# Revit family: 2093120 Sylvania Lighting Fixture MC2 3-6M 4K DALIEM WHT OPAL Recessed
name_source: partatom
category: Lighting Fixtures
revit_build: Autodesk Revit 2016 (Build: 20150220_1215(x64)
units: mm (PartAtom-declared; Revit-internal decimal feet)

## family parameters
Cut with Voids When Loaded = No
Host = Face
Light Source = Yes
OmniClass Number = 23.80.70.11.17
OmniClass Title = Specialized Lighting by Location or Use
Part Type = Normal
Room Calculation Point = No
Round Connector Dimension = Use Diameter
Shared = No

## types (2) — shared parameters
Apparent Load = 66 VA
Assembly Code = D5020200
AssetType = Fixed
Color Filter = 16777215
Description = 2093120   MC2 3.6M 4K DALIEM WHT OPAL  Continuous lines of LED light, white RAL 9016, direct distribution, trimless detail for a seamless finish, suitable for recessed, semi-recessed, surface-mounted or suspended installation either horizontally or vertically, various accessories available, compact and minimalist design based on the Golden Mean, ideal for offices, meeting rooms, corridors, education facilities, museums and libraries, extruded aluminium body, diffuser: opal, colour temperature: 4000K neutral white, total system power: 66W, total fixture output: 6621lm, luminaire efficacy: 100lm/W, LOR: 100%, colour rendering: Ra >80, LED Chromacity: 1 step MacAdam ellipse, lifetime: 60,000 hours at 90% of the original output (L90), energy class: A++, A+, A, IR/UV free light source without heat radiation, operating voltage: 220-240V / 50-60Hz, drive current: 800mA, electronic driver, DALI dimmable, integral emergency: 3 hour maintained, electrical protection: CLASS I, IP20, suitable for internal environment only.
Dimming Lamp Color Temperature Shift = <None>
DocumentationLiterature = http://www.sylvania-lighting.com
DurationUnit = hours
ElectricShockClassification = Class I
Emit Shape Visible in Rendering = No
Emit from Rectangle Length = 3600 mm  [stored 11.811 ft]
Emit from Rectangle Width = 52 mm  [stored 0.170604 ft]
ExpectedLife = 50000
Height_SYL = 86 mm  [stored 0.282152 ft]
IfcExportAs = IfcLightFixtureType
IfcExportType = IfcLightFixtureType
IngressProtection = IP20
Keynote = 16500
Lamp = LED
LampColourRenderingIndex = 80
LampColourTemperature = 4000 K
LampMacAdamStep = 3
LampsType = LED
Length_SYL = 3600 mm  [stored 11.811 ft]
LightOutputRatio = 100
Manufacturer = Feilo Sylvania
ManufacturerName = Feilo Sylvania
Material = aluminium housing, polycarbonate diffuser
Material_1_SYL = Metal_Sylvania_Mini Continuum II_White
Material_2_SYL = Polycarbonate_Sylvania_Mini Continuum II_Opal_4000K
Material_3_SYL = Metal_Sylvania_Mini Contiuum II_Silver
Material_4_SYL = Metal_Sylvania_Mini Contiuum II_Silver
ModelNumber = 2093120
NominalHeight = 86 mm  [stored 0.282152 ft]
NominalLength = 3600 mm  [stored 11.811 ft]
PowerConsumption = 66 W
PowerFactor = 0.98
Tilt Angle = -90.00°
URL = http://www.sylvania-lighting.com
Voltage = 0 V
Weight = 7.8 kg
Width_SYL = 54 mm  [stored 0.177165 ft]
zero-valued in all types: Default Elevation, NominalWidth

## per-type parameters (varying)
| type | LampNominalLuminous | LuminousEfficacy | Model | ModelReference | Name | Photometric Web File | TypeName |
| 2093120 MC2 3.6M 4K DALIEM WHT OPAL Recessed Emergency mode | 121 lm | 1.833 lm/W | MC2 3.6M 4K DALIEM WHT OPAL Recessed Emergency mode | MC2 3.6M 4K DALIEM WHT OPAL Recessed Emergency mode | MC2 3.6M 4K DALIEM WHT OPAL Recessed Emergency mode | 2093120EM.ies | MC2 3.6M 4K DALIEM WHT OPAL Recessed Emergency mode |
| 2093120 MC2 3.6M 4K DALIEM WHT OPAL Recessed | 7020 lm | 106 lm/W | MC2 3.6M 4K DALIEM WHT OPAL Recessed | MC2 3.6M 4K DALIEM WHT OPAL Recessed | MC2 3.6M 4K DALIEM WHT OPAL Recessed | 2093120.ies | MC2 3.6M 4K DALIEM WHT OPAL Recessed |

note: [stored X ft] marks values corroborated as IEEE doubles in the binary element streams (Revit-internal decimal feet)

## geometry (parser evidence)
native form markers: Sweep x2
no freeform markers — native parametric forms only
